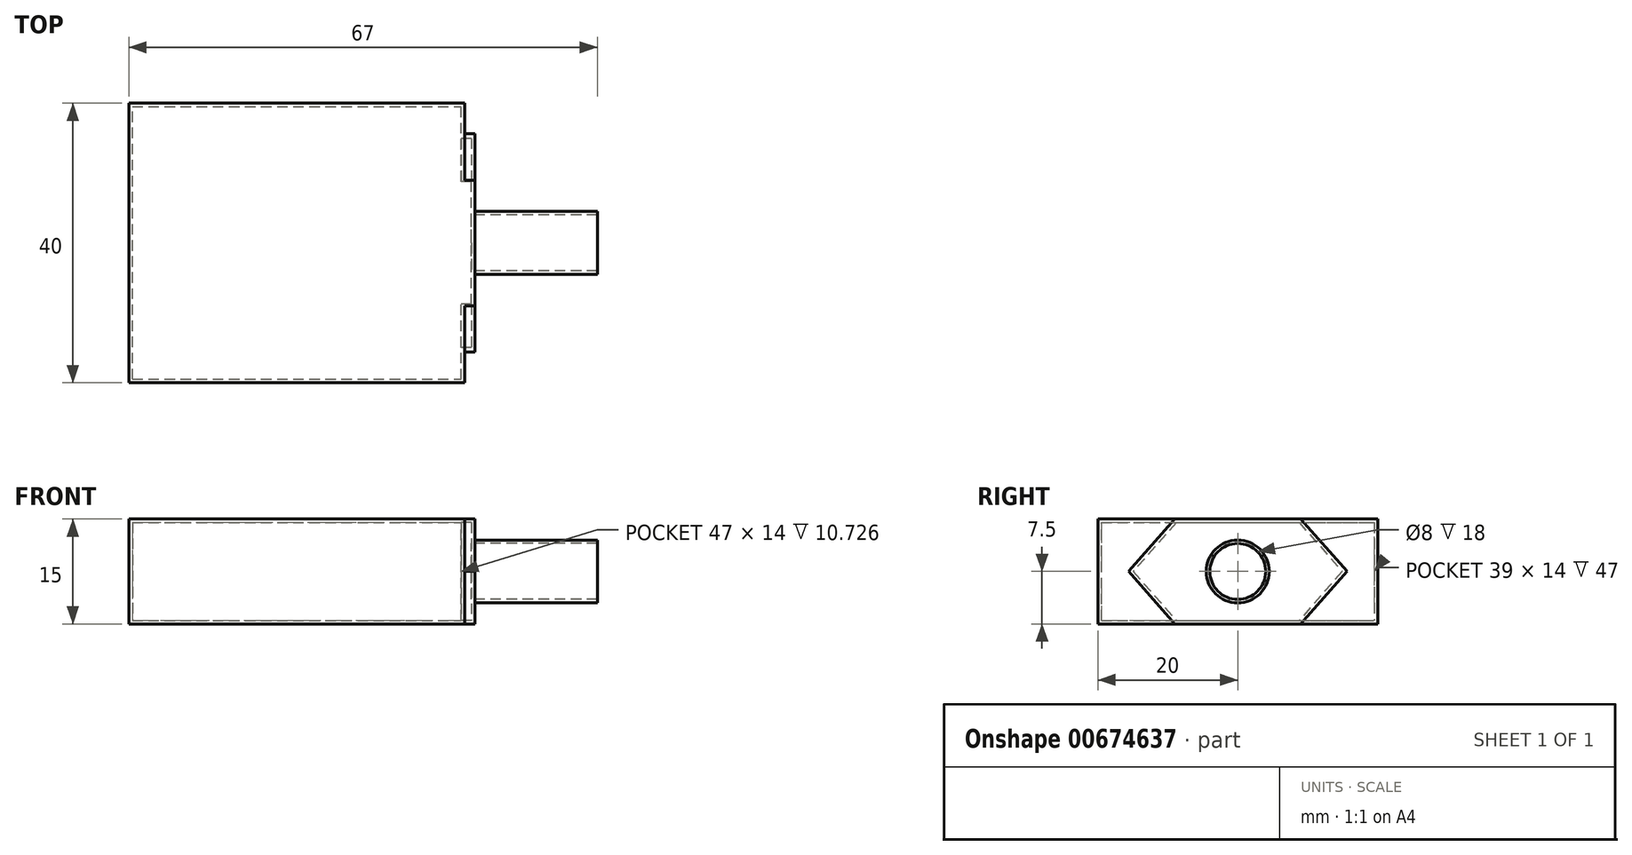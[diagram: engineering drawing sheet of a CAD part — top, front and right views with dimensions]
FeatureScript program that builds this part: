
annotation { "Feature Type Name" : "Feature", "Feature Type Description" : "" }
export const myFeature = defineFeature(function(context is Context, id is Id, definition is map)
    precondition{}
    {
        {
            var Q0;
            Q0=qCreatedBy(makeId("Front.planeOp"),FACE);
            var sketch = newSketch(context, id + "F0", { "sketchPlane" : qUnion([Q0])});
            skLineSegment(sketch, "E0", {"start": v(-22, 15) * mm, "end": v(26, 15) * mm});
            skLineSegment(sketch, "E1", {"start": v(-22, 15) * mm, "end": v(-22, 0) * mm});
            skLineSegment(sketch, "E2", {"start": v(-22, 0) * mm, "end": v(26, 0) * mm});
            skLineSegment(sketch, "E3", {"start": v(26, 0) * mm, "end": v(26, 15) * mm});
            skPoint(sketch, "E4", {"position": v(0, 0) * mm});
            skSolve(sketch);
        }
        {
            var Q0;
            Q0=makeQuery(id+"F0.imprint","IMPRINT",FACE,{"disambiguationData":[TD([[makeQuery(id+"F0.imprint","IMPRINT",EDGE,{"derivedFrom":sQuery(id+"F0.wireOp",EDGE,"E0")}),-1.0]])]});
            extrude(context, id + "F1", {"entities" : qUnion([Q0]), "depth" : 40 * mm, "offsetDistance" : 25 * mm, "symmetric" : true});
        }
        {
            var Q0;
            Q0=makeQuery(id+"F1.opExtrude","SWEPT_FACE",FACE,{"disambiguationData":[OSD([sQuery(id+"F0.wireOp",EDGE,"E3")])]});
            var sketch = newSketch(context, id + "F2", { "sketchPlane" : qUnion([Q0])});
            skLineSegment(sketch, "E5", {"start": v(-9, 0) * mm, "end": v(0, 0) * mm});
            skLineSegment(sketch, "E6", {"start": v(-9, 0) * mm, "end": v(-9, 15) * mm, "construction": true});
            skLineSegment(sketch, "E7", {"start": v(-9, 15) * mm, "end": v(0, 15) * mm});
            skLineSegment(sketch, "E8.MirrorCS", {"start": v(9, 15) * mm, "end": v(0, 15) * mm});
            skLineSegment(sketch, "E9.MirrorCS", {"start": v(9, 0) * mm, "end": v(9, 15) * mm, "construction": true});
            skLineSegment(sketch, "E10.MirrorCS", {"start": v(9, 0) * mm, "end": v(0, 0) * mm});
            skCircle(sketch, "E11", {"center": v(0, 7.5) * mm, "radius": 4.5 * mm});
            skPoint(sketch, "E12", {"position": v(-9, 7.5) * mm});
            skLineSegment(sketch, "E13", {"start": v(-9, 7.5) * mm, "end": v(9, 7.5) * mm, "construction": true});
            skLineSegment(sketch, "E14", {"start": v(-9, 7.5) * mm, "end": v(-15.61, 7.5) * mm, "construction": true});
            skLineSegment(sketch, "E15", {"start": v(-9, 15) * mm, "end": v(-15.61, 7.5) * mm});
            skLineSegment(sketch, "E16", {"start": v(-15.61, 7.5) * mm, "end": v(-9, 0) * mm});
            skLineSegment(sketch, "E17.MirrorCS", {"start": v(9, 15) * mm, "end": v(15.61, 7.5) * mm});
            skLineSegment(sketch, "E18.MirrorCS", {"start": v(9, 7.5) * mm, "end": v(15.61, 7.5) * mm, "construction": true});
            skLineSegment(sketch, "E19.MirrorCS", {"start": v(15.61, 7.5) * mm, "end": v(9, 0) * mm});
            skSolve(sketch);
        }
        {
            var Q0;
            Q0=makeQuery(id+"F2.imprint","IMPRINT",FACE,{"disambiguationData":[TD([[makeQuery(id+"F2.imprint","IMPRINT",EDGE,{"derivedFrom":sQuery(id+"F2.wireOp",EDGE,"E5")}),1.0]])]});
            extrude(context, id + "F3", {"entities" : qUnion([Q0]), "operationType" : NewBodyOperationType.ADD, "depth" : 1.5 * mm, "offsetDistance" : 25 * mm});
        }
        {
            var Q0;
            Q0=makeQuery(id+"F3.boolean.opBoolean","SPLIT",FACE,{"disambiguationData":[TD([makeQuery(id+"F3.opExtrude","SWEPT_FACE",FACE,{"disambiguationData":[OSD([sQuery(id+"F2.wireOp",EDGE,"E11")])]})])],"derivedFrom":makeQuery(id+"F1.opExtrude","SWEPT_FACE",FACE,{"disambiguationData":[OSD([sQuery(id+"F0.wireOp",EDGE,"E3")])]})});
            extrude(context, id + "F4", {"entities" : qUnion([Q0]), "operationType" : NewBodyOperationType.ADD, "depth" : 19 * mm, "offsetDistance" : 25 * mm});
        }
        {
            var Q0;
            Q0=makeQuery(id+"F4.opExtrude","CAP_FACE",FACE,{"disambiguationData":[OSD([sQuery(id+"F0.wireOp",EDGE,"E3")])],"isStart":false});
            shell(context, id + "F5", {"entities" : qUnion([Q0]), "thickness" : .5 * mm});
        }
    });
